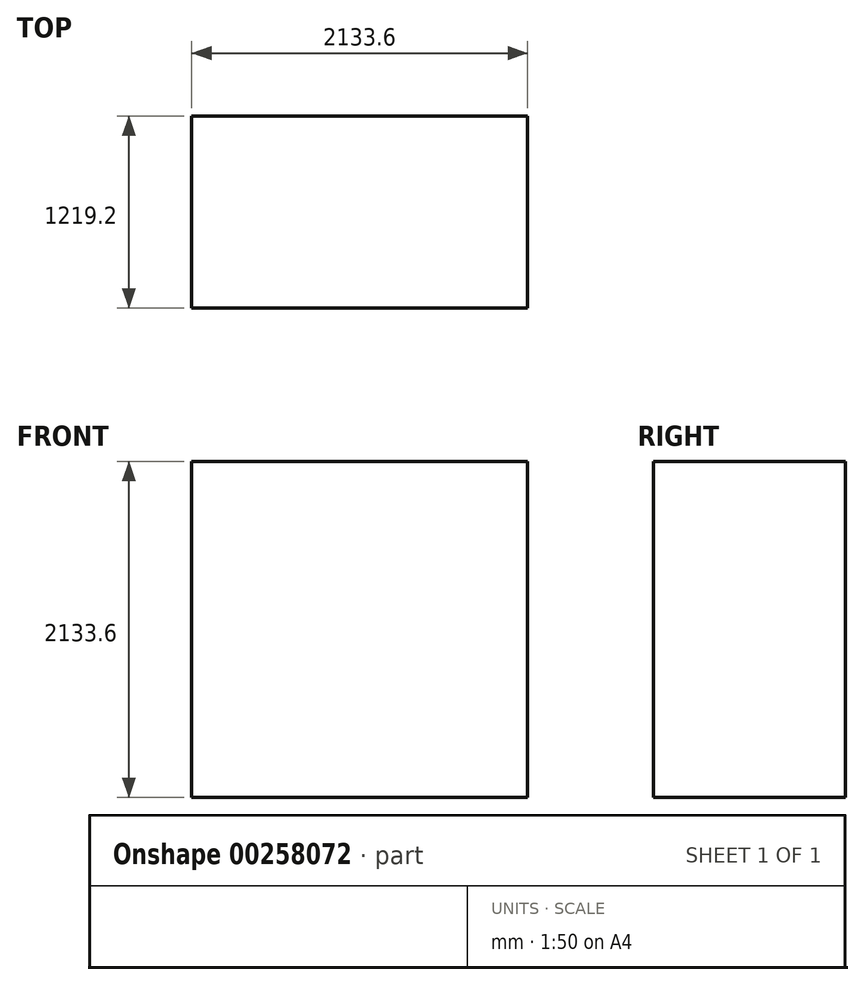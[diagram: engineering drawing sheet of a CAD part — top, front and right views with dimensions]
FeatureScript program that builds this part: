
annotation { "Feature Type Name" : "Feature", "Feature Type Description" : "" }
export const myFeature = defineFeature(function(context is Context, id is Id, definition is map)
    precondition{}
    {
        {
            var Q0;
            Q0=qCreatedBy(makeId("Top.planeOp"),FACE);
            var sketch = newSketch(context, id + "F0", { "sketchPlane" : qUnion([Q0])});
            skLineSegment(sketch, "E0.bottom", {"start": v(1066.8, -609.6) * mm, "end": v(-1066.8, -609.6) * mm});
            skLineSegment(sketch, "E0.top", {"start": v(1066.8, 609.6) * mm, "end": v(-1066.8, 609.6) * mm});
            skLineSegment(sketch, "E0.left", {"start": v(1066.8, -609.6) * mm, "end": v(1066.8, 609.6) * mm});
            skLineSegment(sketch, "E0.right", {"start": v(-1066.8, -609.6) * mm, "end": v(-1066.8, 609.6) * mm});
            skPoint(sketch, "E0.middle", {"position": v(0, 0) * mm});
            skSolve(sketch);
        }
        {
            var Q0;
            Q0 = qSketchRegion(id + "F0", true);
            extrude(context, id + "F1", {"entities" : qUnion([Q0]), "depth" : 2133.6 * mm});
        }
    });
